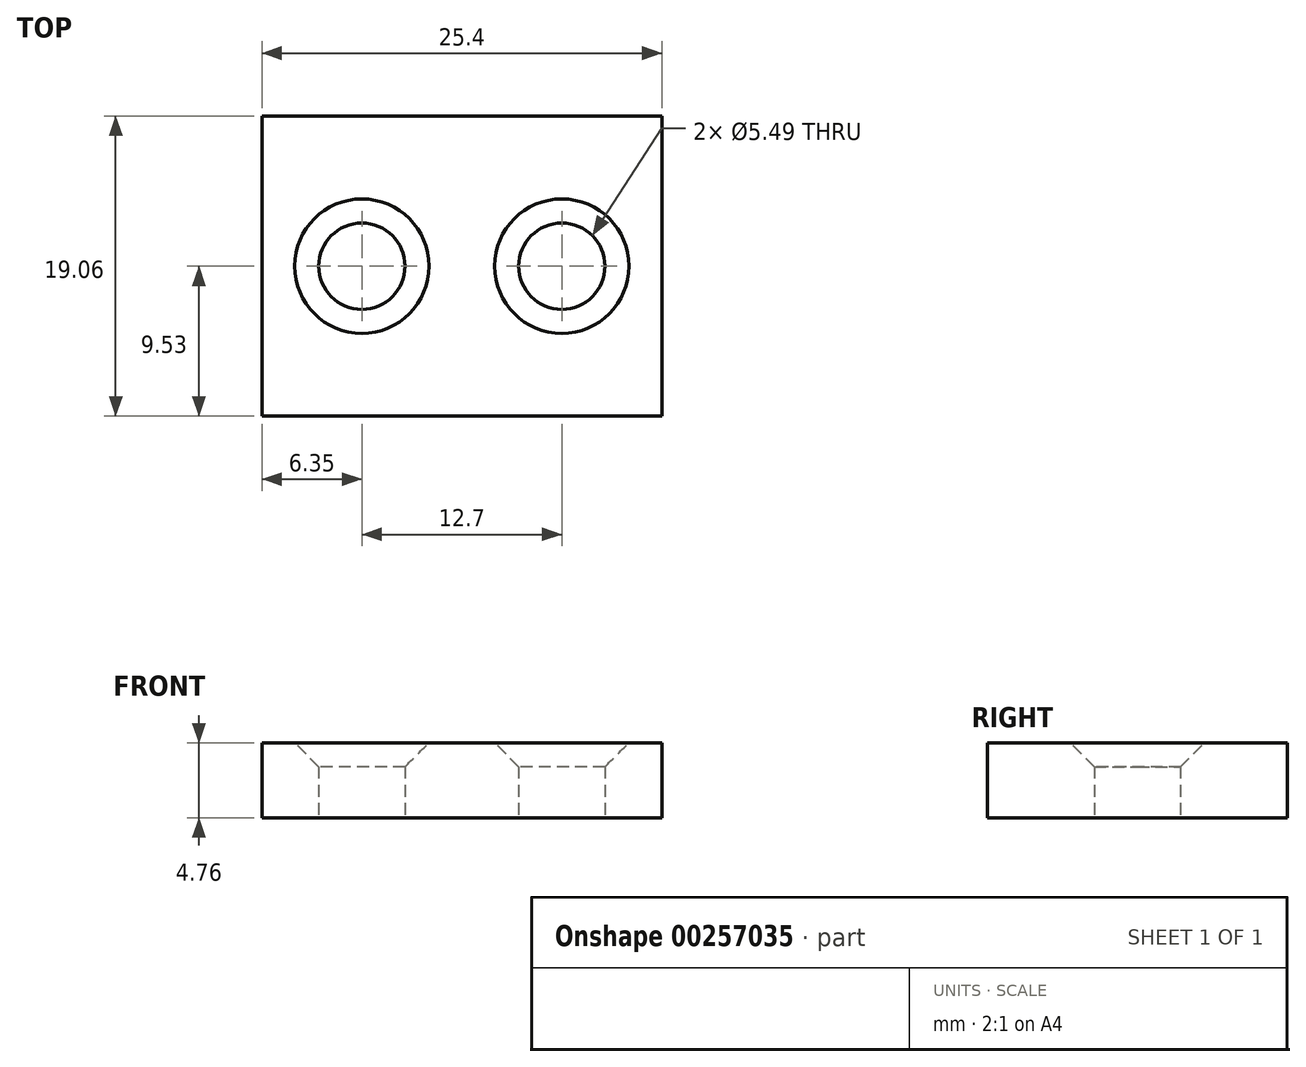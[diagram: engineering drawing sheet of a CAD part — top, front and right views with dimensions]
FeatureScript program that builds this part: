
annotation { "Feature Type Name" : "Feature", "Feature Type Description" : "" }
export const myFeature = defineFeature(function(context is Context, id is Id, definition is map)
    precondition{}
    {
        {
            var Q0;
            Q0=qCreatedBy(makeId("Top.planeOp"),FACE);
            var sketch = newSketch(context, id + "F0", { "sketchPlane" : qUnion([Q0])});
            skLineSegment(sketch, "E0.bottom", {"start": v(12.7, 9.53) * mm, "end": v(-12.7, 9.52) * mm});
            skLineSegment(sketch, "E0.top", {"start": v(12.7, -9.52) * mm, "end": v(-12.7, -9.53) * mm});
            skLineSegment(sketch, "E0.left", {"start": v(12.7, 9.53) * mm, "end": v(12.7, -9.52) * mm});
            skLineSegment(sketch, "E0.right", {"start": v(-12.7, 9.52) * mm, "end": v(-12.7, -9.52) * mm});
            skPoint(sketch, "E0.middle", {"position": v(0, 0) * mm});
            skCircle(sketch, "E1", {"center": v(-6.35, 0) * mm, "radius": 2.74 * mm});
            skCircle(sketch, "E2", {"center": v(6.35, 0) * mm, "radius": 2.74 * mm});
            skSolve(sketch);
        }
        {
            var Q0;
            Q0 = qSketchRegion(id + "F0", true);
            extrude(context, id + "F1", {"entities" : qUnion([Q0]), "depth" : 4.76 * mm});
        }
        {
            var Q0;
            Q0=makeQuery(id+"F1.opExtrude","CAP_EDGE",EDGE,{"disambiguationData":[OSD([sQuery(id+"F0.wireOp",EDGE,"E1")])],"isStart":false});
            var Q1;
            Q1=makeQuery(id+"F1.opExtrude","CAP_EDGE",EDGE,{"disambiguationData":[OSD([sQuery(id+"F0.wireOp",EDGE,"E2")])],"isStart":false});
            chamfer(context, id + "F2", {"entities" : qUnion([Q0, Q1]), "width" : 1.52 * mm, "tangentPropagation" : true});
        }
    });
